# Revit family: Table-Teknion-PCMR_Mits_Round-R2019
name_source: partatom
category: Furniture
units: mm (PartAtom-declared; Revit-internal decimal feet)

## family parameters
Always vertical = Yes
Cut with Voids When Loaded = No
OmniClass Number = 23.40.20.00
OmniClass Title = General Furniture and Specialties
Room Calculation Point = No
Shared = Yes
Work Plane-Based = No

## types (3) — shared parameters
Assembly Code = E2020200
Manufacturer = StudioTK
Manufacturer Fax = 919-464-2927
Part Number = PCMR
Product Documentation Link = https://assets.teknion.com
Product Line = Punt
Product Page URL = https://www.studiotk.com
Series = Punt
Sustainability Data = http://www.studiotk.com
URL = www.studiotk.com
Warranty = https://d2r72yk5wmppdj.cloudfront.net

## per-type parameters (varying)
| type | Description | Diameter | Inner Diameter | Leg Width | Model |
| 29" Height, 42" Diameter | Mitis Round Table, 29" Height, 42" Diameter | 42 " | 33.103 " | 15.414 " | PCMR2942 |
| 29" Height, 48" Diameter | Mitis Round Table, 29" Height, 48" Diameter | 48 " | 39.228 " | 18.399 " | PCMR2948 |
| 29" Height, 54" Diameter | Mitis Round Table, 29" Height, 54" Diameter | 54 " | 45.228 " | 21.399 " | PCMR2954 |

## geometry (parser evidence)
native form markers: Sweep x5
no freeform markers — native parametric forms only
